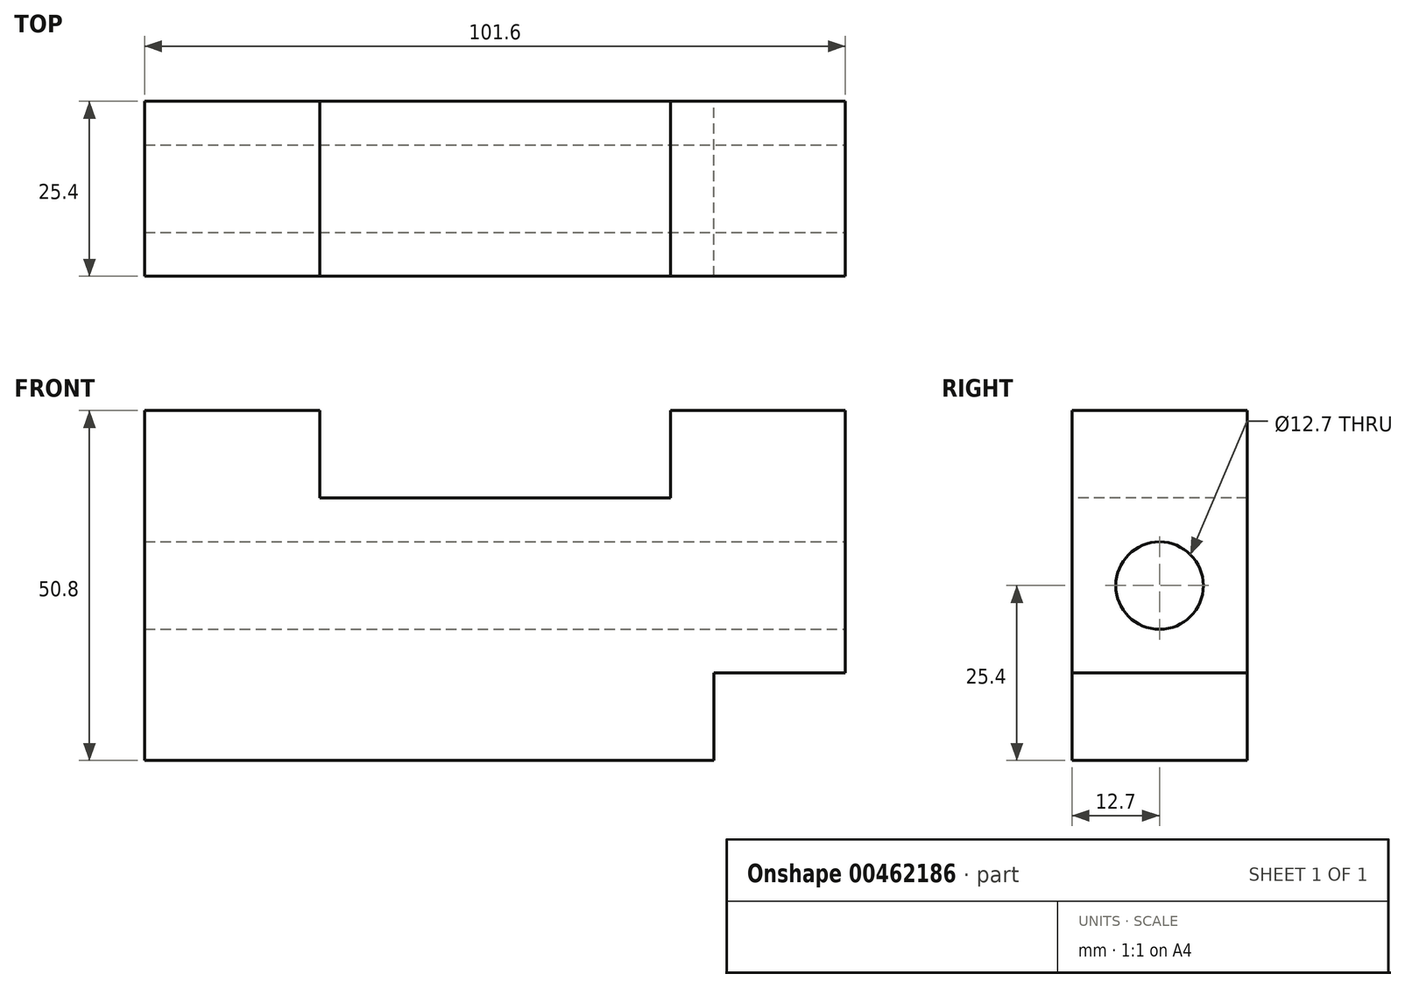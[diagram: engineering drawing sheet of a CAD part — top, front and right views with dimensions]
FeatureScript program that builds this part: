
annotation { "Feature Type Name" : "Feature", "Feature Type Description" : "" }
export const myFeature = defineFeature(function(context is Context, id is Id, definition is map)
    precondition{}
    {
        {
            var Q0;
            Q0=qCreatedBy(makeId("Front.planeOp"),FACE);
            var sketch = newSketch(context, id + "F0", { "sketchPlane" : qUnion([Q0])});
            skLineSegment(sketch, "E0.bottom", {"start": v(-50.8, 25.4) * mm, "end": v(50.8, 25.4) * mm});
            skLineSegment(sketch, "E0.top", {"start": v(-50.8, -25.4) * mm, "end": v(50.8, -25.4) * mm});
            skLineSegment(sketch, "E0.left", {"start": v(-50.8, 25.4) * mm, "end": v(-50.8, -25.4) * mm});
            skLineSegment(sketch, "E0.right", {"start": v(50.8, 25.4) * mm, "end": v(50.8, -25.4) * mm});
            skPoint(sketch, "E0.middle", {"position": v(0, 0) * mm});
            skSolve(sketch);
        }
        {
            var Q0;
            Q0=makeQuery(id+"F0.imprint","IMPRINT",FACE,{"disambiguationData":[TD([[makeQuery(id+"F0.imprint","IMPRINT",EDGE,{"derivedFrom":sQuery(id+"F0.wireOp",EDGE,"E0.bottom")}),-1.0]])]});
            extrude(context, id + "F1", {"entities" : qUnion([Q0]), "depth" : 25.4 * mm});
        }
        {
            var Q0;
            Q0=makeQuery(id+"F1.opExtrude","CAP_FACE",FACE,{"disambiguationData":[OSD([sQuery(id+"F0.wireOp",EDGE,"E0.bottom"),sQuery(id+"F0.wireOp",EDGE,"E0.top"),sQuery(id+"F0.wireOp",EDGE,"E0.left"),sQuery(id+"F0.wireOp",EDGE,"E0.right")])],"isStart":false});
            var sketch = newSketch(context, id + "F2", { "sketchPlane" : qUnion([Q0])});
            skLineSegment(sketch, "E1.bottom", {"start": v(-25.37, 25.4) * mm, "end": v(25.43, 25.4) * mm});
            skLineSegment(sketch, "E1.top", {"start": v(-25.37, 12.7) * mm, "end": v(25.43, 12.7) * mm});
            skLineSegment(sketch, "E1.left", {"start": v(-25.37, 25.4) * mm, "end": v(-25.37, 12.7) * mm});
            skLineSegment(sketch, "E1.right", {"start": v(25.43, 25.4) * mm, "end": v(25.43, 12.7) * mm});
            skSolve(sketch);
        }
        {
            var Q0;
            Q0=makeQuery(id+"F1.opExtrude","SWEPT_FACE",FACE,{"disambiguationData":[OSD([sQuery(id+"F0.wireOp",EDGE,"E0.right")])]});
            var sketch = newSketch(context, id + "F3", { "sketchPlane" : qUnion([Q0])});
            skLineSegment(sketch, "E2.bottom", {"start": v(-25.4, -25.4) * mm, "end": v(0, -25.4) * mm});
            skLineSegment(sketch, "E2.top", {"start": v(-25.4, -12.7) * mm, "end": v(0, -12.7) * mm});
            skLineSegment(sketch, "E2.left", {"start": v(-25.4, -25.4) * mm, "end": v(-25.4, -12.7) * mm});
            skLineSegment(sketch, "E2.right", {"start": v(0, -25.4) * mm, "end": v(0, -12.7) * mm});
            skSolve(sketch);
        }
        {
            var Q0;
            Q0=makeQuery(id+"F2.imprint","IMPRINT",FACE,{"disambiguationData":[TD([[makeQuery(id+"F2.imprint","IMPRINT",EDGE,{"derivedFrom":sQuery(id+"F2.wireOp",EDGE,"E1.bottom")}),-1.0]])]});
            extrude(context, id + "F4", {"entities" : qUnion([Q0]), "operationType" : NewBodyOperationType.REMOVE, "oppositeDirection" : true, "depth" : 25.4 * mm});
        }
        {
            var Q0;
            Q0=makeQuery(id+"F3.imprint","IMPRINT",FACE,{"disambiguationData":[TD([[makeQuery(id+"F3.imprint","IMPRINT",EDGE,{"derivedFrom":sQuery(id+"F3.wireOp",EDGE,"E2.bottom")}),1.0]])]});
            extrude(context, id + "F5", {"entities" : qUnion([Q0]), "operationType" : NewBodyOperationType.REMOVE, "oppositeDirection" : true, "depth" : 19.05 * mm});
        }
        {
            var Q0;
            Q0=makeQuery(id+"F1.opExtrude","SWEPT_FACE",FACE,{"disambiguationData":[OSD([sQuery(id+"F0.wireOp",EDGE,"E0.right")])]});
            var sketch = newSketch(context, id + "F6", { "sketchPlane" : qUnion([Q0])});
            skCircle(sketch, "E3", {"center": v(-12.7, 0) * mm, "radius": 6.35 * mm});
            skSolve(sketch);
        }
        {
            var Q0;
            Q0=makeQuery(id+"F6.imprint","IMPRINT",FACE,{"disambiguationData":[TD([[makeQuery(id+"F6.imprint","IMPRINT",EDGE,{"derivedFrom":sQuery(id+"F6.wireOp",EDGE,"E3")}),1.0]])]});
            extrude(context, id + "F7", {"entities" : qUnion([Q0]), "operationType" : NewBodyOperationType.REMOVE, "oppositeDirection" : true, "depth" : 101.6 * mm});
        }
    });
